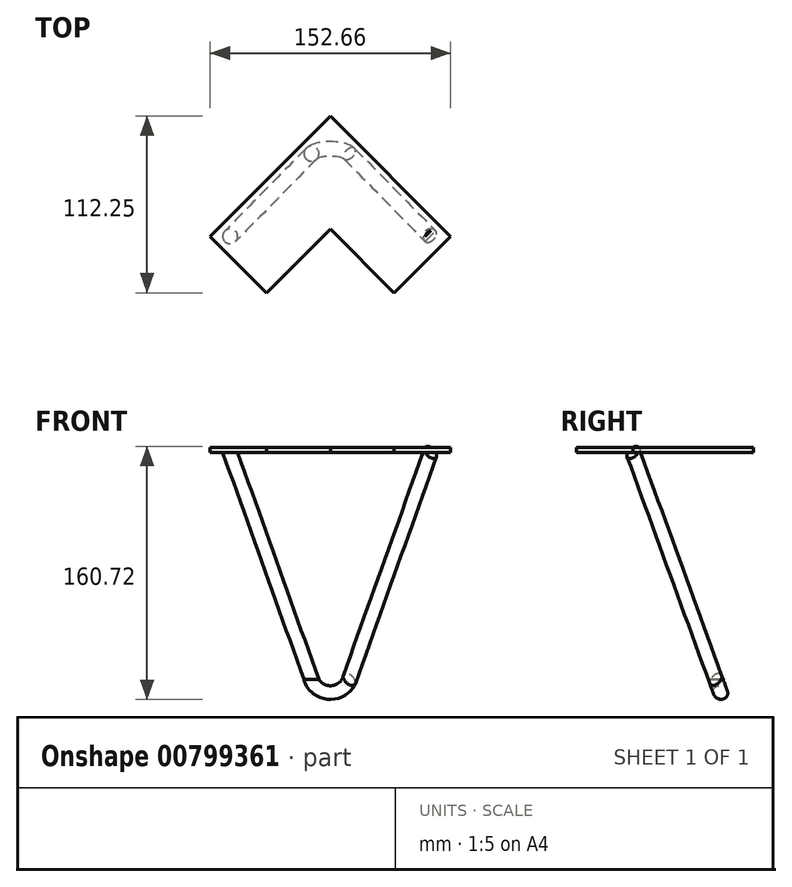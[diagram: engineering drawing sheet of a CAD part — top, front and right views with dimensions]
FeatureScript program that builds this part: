
annotation { "Feature Type Name" : "Feature", "Feature Type Description" : "" }
export const myFeature = defineFeature(function(context is Context, id is Id, definition is map)
    precondition{}
    {
        {
            var Q0;
            Q0=qCreatedBy(makeId("Top.planeOp"),FACE);
            var sketch = newSketch(context, id + "F0", { "sketchPlane" : qUnion([Q0])});
            skLineSegment(sketch, "E0", {"start": v(0, 0) * mm, "end": v(0, 76.33) * mm, "construction": true});
            skLineSegment(sketch, "E1", {"start": v(0, 76.33) * mm, "end": v(-76.33, 0) * mm});
            skLineSegment(sketch, "E2", {"start": v(0, 76.33) * mm, "end": v(76.33, 0) * mm});
            skLineSegment(sketch, "E3", {"start": v(76.33, 0) * mm, "end": v(40.41, -35.92) * mm});
            skLineSegment(sketch, "E4", {"start": v(40.41, -35.92) * mm, "end": v(0, 4.5) * mm});
            skLineSegment(sketch, "E5.MirrorCS", {"start": v(-40.41, -35.92) * mm, "end": v(0, 4.5) * mm});
            skLineSegment(sketch, "E6.MirrorCS", {"start": v(-76.33, 0) * mm, "end": v(-40.41, -35.92) * mm});
            skSolve(sketch);
        }
        {
            var Q0;
            Q0 = qSketchRegion(id + "F0", true);
            extrude(context, id + "F1", {"entities" : qUnion([Q0]), "depth" : 3.17 * mm, "offsetDistance" : 25.4 * mm});
        }
        {
            var Q0;
            Q0=qCreatedBy(makeId("Top.planeOp"),FACE);
            cPlane(context, id + "F2", {"entities" : qUnion([Q0]), "cplaneType" : CPlaneType.OFFSET, "offset" : 152.4 * mm, "oppositeDirection" : true, "width" : 152.4 * mm, "height" : 152.4 * mm});
        }
        {
            var Q0;
            Q0=qCreatedBy(makeId("Right.planeOp"),FACE);
            var sketch = newSketch(context, id + "F3", { "sketchPlane" : qUnion([Q0])});
            skLineSegment(sketch, "E7", {"start": v(0, 0) * mm, "end": v(55.47, -152.4) * mm});
            skSolve(sketch);
        }
        {
            var Q0;
            Q0=sQuery(id+"F3.wireOp",EDGE,"E7");
            var Q1;
            Q1=qCreatedBy(makeId("Top.planeOp"),FACE);
            cPlane(context, id + "F4", {"entities" : qUnion([Q0, Q1]), "cplaneType" : CPlaneType.LINE_ANGLE, "offset" : 25.4 * mm, "angle" : 0 * degree, "width" : 152.4 * mm, "height" : 152.4 * mm});
        }
        {
            var Q0;
            Q0=qCreatedBy(id+"F4.planeOp",FACE);
            var sketch = newSketch(context, id + "F5", { "sketchPlane" : qUnion([Q0])});
            skLineSegment(sketch, "E8", {"start": v(0, 0) * mm, "end": v(0, -189.35) * mm, "construction": true});
            skLineSegment(sketch, "E9", {"start": v(-63.63, 0) * mm, "end": v(-12.04, -153.53) * mm});
            skLineSegment(sketch, "E10.MirrorCS", {"start": v(63.63, 0) * mm, "end": v(12.04, -153.53) * mm});
            skPoint(sketch, "E11.visualSharp", {"position": v(0, -189.35) * mm});
            skArc(sketch, "E11.filletArc", {"start": v(-12.04, -153.53) * mm, "mid": v(0, -162.18) * mm, "end": v(12.04, -153.53) * mm});
            skSolve(sketch);
        }
        {
            var Q0;
            Q0=makeQuery(id+"F1.opExtrude","CAP_FACE",FACE,{"disambiguationData":[OSD([sQuery(id+"F0.wireOp",EDGE,"E1"),sQuery(id+"F0.wireOp",EDGE,"E2"),sQuery(id+"F0.wireOp",EDGE,"E3"),sQuery(id+"F0.wireOp",EDGE,"E4"),sQuery(id+"F0.wireOp",EDGE,"E5.MirrorCS"),sQuery(id+"F0.wireOp",EDGE,"E6.MirrorCS")])],"isStart":true});
            var sketch = newSketch(context, id + "F6", { "sketchPlane" : qUnion([Q0])});
            skCircle(sketch, "E12", {"center": v(-63.63, 0) * mm, "radius": 4.76 * mm});
            skSolve(sketch);
        }
        {
            var Q0;
            Q0=makeQuery(id+"F6.imprint","IMPRINT",FACE,{"disambiguationData":[TD([[makeQuery(id+"F6.imprint","IMPRINT",EDGE,{"derivedFrom":sQuery(id+"F6.wireOp",EDGE,"E12")}),1.0]])]});
            var Q1;
            Q1=sQuery(id+"F5.wireOp",EDGE,"E9");
            var Q2;
            Q2=sQuery(id+"F5.wireOp",EDGE,"E11.filletArc");
            var Q3;
            Q3=sQuery(id+"F5.wireOp",EDGE,"E10.MirrorCS");
            sweep(context, id + "F7", {"operationType" : NewBodyOperationType.ADD, "profiles" : qUnion([Q0]), "path" : qUnion([Q1, Q2, Q3])});
        }
    });
